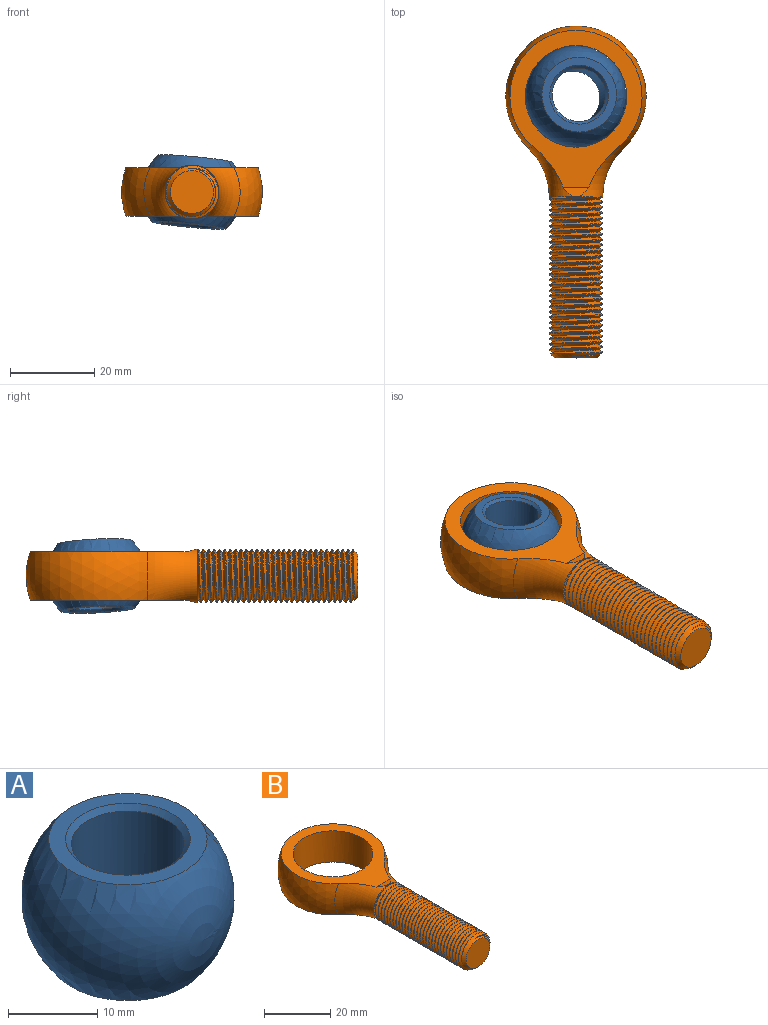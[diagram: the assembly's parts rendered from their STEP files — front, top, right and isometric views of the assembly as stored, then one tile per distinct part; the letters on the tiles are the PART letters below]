
ASSEMBLY  parts=2 mates=1
PART A: 6 faces, bbox 23.8x23.8x23.8 mm
  f0: sphere r=11.91mm, area 1187.6mm2, adj f1,f2
  f1: plane 17.75x17.75mm, normal (0,0,1), area 94.1mm2, adj f0,f5
  f2: plane 17.75x17.75mm, normal (0,0,-1), area 94.1mm2, adj f0,f4
  f3: cylinder r=6.35mm len=14.61mm, axis (0,0,1), area 582.7mm2, adj f4,f5
  f4: cone r=6.99mm half-angle=45deg, axis (0,0,-1), area 37.6mm2, adj f2,f3
  f5: cone r=6.35mm half-angle=45deg, axis (0,0,1), area 37.6mm2, adj f1,f3
PART B: 15 faces, bbox 49.1x79.8x49.1 mm
  f0: torus R=22.32mm, axis (0,-1,0), area 180.4mm2, adj f8,f9,f10,f11,f12,f13
  f1: cone r=6.35mm half-angle=45deg, axis (0,1,0), area 42.4mm2, adj f2,f3,f4,f5,f6
  f2: plane 10.16x10.16mm, normal (0,-1,0), area 81.1mm2, adj f1
  f3: cylinder r=6.35mm len=36.83mm, axis (0,1,0), area 183.9mm2, adj f1,f4,f6,f7
  f4: bspline ~39.05x12.7mm, area 1045.8mm2, adj f1,f3,f5,f9
  f5: cylinder r=5.53mm len=37.66mm, axis (0,1,0), area 165.1mm2, adj f1,f4,f6,f9
  f6: bspline ~38.26x12.7mm, area 1045.6mm2, adj f1,f3,f5,f9
  f7: torus R=22.32mm, axis (0,-1,0), area 180.4mm2, adj f3,f8,f9,f10,f11,f12,f13
  f8: sphere r=16.67mm, area 925.3mm2, adj f0,f7,f10,f12
  f9: plane 13.21x13.21mm, normal (0,-1,0), area 15.7mm2, adj f0,f4,f5,f6,f7
  f10: plane 37.68x31.81mm, normal (0,0,1), area 376.1mm2, adj f0,f7,f8,f11,f14
  f11: plane 6.9x3.08mm, normal (0,0.25,0.97), area 9.3mm2, adj f0,f7,f10
  f12: plane 37.68x31.81mm, normal (0,0,-1), area 376.1mm2, adj f0,f7,f8,f13,f14
  f13: plane 6.9x3.08mm, normal (0,0.25,-0.97), area 9.3mm2, adj f0,f7,f12
  f14: cylinder r=12.03mm len=24.05mm, axis (0,0,1), area 869.6mm2, adj f10,f12
PLACE A rot(axis=(-0.43,0.75,-0.5),7.2deg) t=(-1.43,0.08,1.36)mm
PLACE B at identity fixed
MATE ball A.f3 <-> B.f14  axis (0.1,0.05,0.99) through (0,23.81,0)mm
